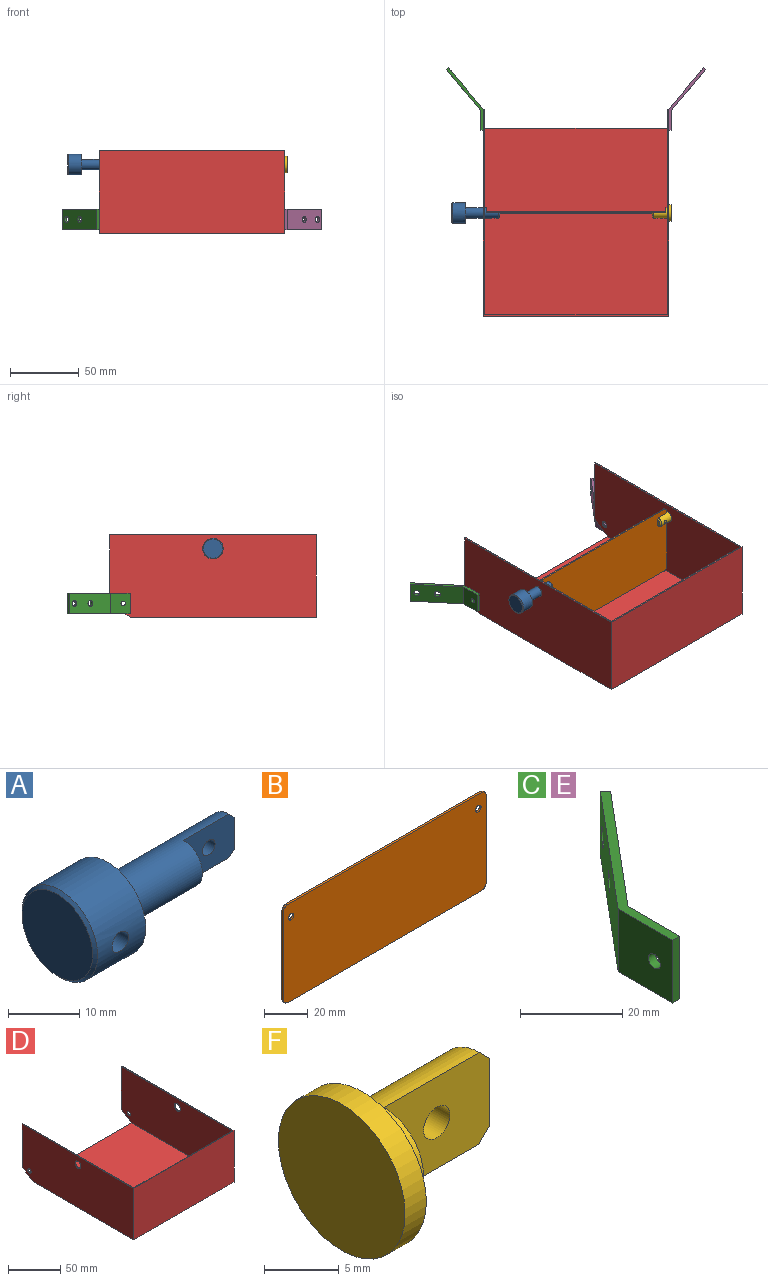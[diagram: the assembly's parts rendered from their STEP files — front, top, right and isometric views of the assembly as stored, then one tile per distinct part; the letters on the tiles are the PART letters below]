
ASSEMBLY  parts=6 mates=5
PART A: 12 faces, bbox 35x15x15 mm
  f0: cylinder r=7.5mm len=15mm, axis (-1,0,0), area 439.1mm2, adj f2,f9,f11
  f1: cylinder r=3.75mm len=24mm, axis (-1,0,0), area 454.5mm2, adj f2,f5,f6,f7,f8
  f2: plane 15x15mm, normal (1,0,0), area 132.5mm2, adj f0,f1
  f3: plane 14x14mm, normal (-1,0,0), area 153.9mm2, adj f11
  f4: plane 5.5x2.75mm, normal (1,0,0), area 11.9mm2, adj f5,f7
  f5: cone r=2.75mm half-angle=45deg, axis (-1,0,0), area 14.4mm2, adj f1,f4,f7
  f6: plane 7.5x3.75mm, normal (1,0,0), area 22.1mm2, adj f1,f7
  f7: plane 10x7.5mm, normal (0,-1,0), area 69.1mm2, adj f1,f4,f5,f6,f8
  f8: cylinder r=1.25mm len=3.75mm, axis (0,-1,0), area 28.6mm2, adj f1,f7
  f9: cylinder r=1.65mm len=7.5mm, axis (0,1,0), area 76.8mm2, adj f0,f10
  f10: plane 3.3x3.3mm, normal (0,-1,0), area 8.6mm2, adj f9
  f11: cone r=7.5mm half-angle=45deg, axis (1,0,0), area 32.2mm2, adj f0,f3
PART B: 12 faces, bbox 131x1x55 mm
  f0: plane 49x1mm, normal (-1,0,0), area 49mm2, adj f4,f5,f6,f9
  f1: plane 125x1mm, normal (0,0,-1), area 125mm2, adj f4,f5,f6,f7
  f2: plane 49x1mm, normal (1,0,0), area 49mm2, adj f4,f5,f7,f8
  f3: plane 125x1mm, normal (0,0,1), area 125mm2, adj f4,f5,f8,f9
  f4: plane 131x55mm, normal (0,-1,0), area 7178mm2, adj f0,f1,f2,f3,f6,f7,f8,f9
  f5: plane 131x55mm, normal (0,1,0), area 7178mm2, adj f0,f1,f2,f3,f6,f7,f8,f9
  f6: cylinder r=3mm len=3mm, axis (0,-1,0), area 4.7mm2, adj f0,f1,f4,f5
  f7: cylinder r=3mm len=3mm, axis (0,-1,0), area 4.7mm2, adj f1,f2,f4,f5
  f8: cylinder r=3mm len=3mm, axis (0,1,0), area 4.7mm2, adj f2,f3,f4,f5
  f9: cylinder r=3mm len=3mm, axis (0,1,0), area 4.7mm2, adj f0,f3,f4,f5
  f10: cylinder r=1.75mm len=3.5mm, axis (0,-1,0), area 11mm2, adj f4,f5
  f11: cylinder r=1.75mm len=3.5mm, axis (0,-1,0), area 11mm2, adj f4,f5
PART C: 11 faces, bbox 27.2x45.6x15 mm
  f0: plane 15x2mm, normal (0,-1,0), area 30mm2, adj f1,f5,f6,f7
  f1: plane 15x14.27mm, normal (1,0,0), area 205.5mm2, adj f0,f2,f6,f7,f8
  f2: plane 30.08x25.24mm, normal (0.77,-0.64,0), area 558.7mm2, adj f1,f3,f6,f7,f9,f10
  f3: plane 15x1.53mm, normal (0.64,0.77,0), area 30mm2, adj f2,f4,f6,f7
  f4: plane 30.64x25.71mm, normal (-0.77,0.64,0), area 569.6mm2, adj f3,f5,f6,f7,f9,f10
  f5: plane 15x15mm, normal (-1,0,0), area 216.4mm2, adj f0,f4,f6,f7,f8
  f6: plane 45.64x27.24mm, normal (0,0,1), area 108.5mm2, adj f0,f1,f2,f3,f4,f5
  f7: plane 45.64x27.24mm, normal (0,0,-1), area 108.5mm2, adj f0,f1,f2,f3,f4,f5
  f8: cylinder r=1.65mm len=3.3mm, axis (1,0,0), area 20.7mm2, adj f1,f5
  f9: cylinder r=2.2mm len=4.66mm, axis (0.77,-0.64,0), area 27.6mm2, adj f2,f4
  f10: cylinder r=2.2mm len=4.66mm, axis (0.77,-0.64,0), area 27.6mm2, adj f2,f4
PART D: 16 faces, bbox 135x151x60 mm
  f0: plane 136x135mm, normal (0,0,-1), area 18360mm2, adj f1,f5,f10,f15
  f1: plane 151x60mm, normal (1,0,0), area 8918.8mm2, adj f0,f7,f8,f10,f11,f13,f15
  f2: plane 150x59mm, normal (-1,0,0), area 8723.1mm2, adj f3,f7,f8,f9,f11,f13,f15
  f3: plane 136.5x133mm, normal (0,0,1), area 18154.5mm2, adj f2,f4,f9,f15
  f4: plane 150x59mm, normal (1,0,0), area 8723.1mm2, adj f3,f6,f8,f9,f12,f14,f15
  f5: plane 151x60mm, normal (-1,0,0), area 8918.8mm2, adj f0,f6,f8,f10,f12,f14,f15
  f6: plane 50x1mm, normal (0,1,0), area 50mm2, adj f4,f5,f8,f15
  f7: plane 50x1mm, normal (0,1,0), area 50mm2, adj f1,f2,f8,f15
  f8: plane 151x135mm, normal (0,0,1), area 435mm2, adj f1,f2,f4,f5,f6,f7,f9,f10
  f9: plane 133x59mm, normal (0,1,0), area 7847mm2, adj f2,f3,f4,f8
  f10: plane 135x60mm, normal (0,-1,0), area 8100mm2, adj f0,f1,f5,f8
  f11: cylinder r=2.25mm len=4.5mm, axis (-1,0,0), area 14.1mm2, adj f1,f2
  f12: cylinder r=2.25mm len=4.5mm, axis (-1,0,0), area 14.1mm2, adj f4,f5
  f13: cylinder r=4mm len=8mm, axis (-1,0,0), area 25.1mm2, adj f1,f2
  f14: cylinder r=4mm len=8mm, axis (-1,0,0), area 25.1mm2, adj f4,f5
  f15: plane 135x15mm, normal (0,0.55,-0.83), area 275.8mm2, adj f0,f1,f2,f3,f4,f5,f6,f7
PART E: same geometry as C
PART F: 9 faces, bbox 14x12x12 mm
  f0: cylinder r=3.75mm len=11mm, axis (-1,0,0), area 148.2mm2, adj f2,f5,f6,f7,f8
  f1: cylinder r=6mm len=12mm, axis (-1,0,0), area 75.4mm2, adj f2,f3
  f2: plane 12x12mm, normal (1,0,0), area 68.9mm2, adj f0,f1
  f3: plane 12x12mm, normal (-1,0,0), area 113.1mm2, adj f1
  f4: plane 5.5x2.75mm, normal (1,0,0), area 11.9mm2, adj f6,f8
  f5: plane 7.5x3.75mm, normal (1,0,0), area 22.1mm2, adj f0,f6
  f6: plane 10x7.5mm, normal (0,-1,0), area 69.1mm2, adj f0,f4,f5,f7,f8
  f7: cylinder r=1.25mm len=3.75mm, axis (0,-1,0), area 28.6mm2, adj f0,f6
  f8: cone r=2.75mm half-angle=45deg, axis (-1,0,0), area 14.4mm2, adj f0,f4,f6
PLACE A rot(axis=(1,0,0),180deg) t=(-90.5,7.5,50)mm
PLACE B t=(0,8.5,30.5)mm
PLACE C rot(axis=(0,1,0),180deg) t=(-69.5,75.65,10)mm
PLACE D t=(0,83,20)mm
PLACE E t=(69.5,75.65,10)mm
PLACE F rot(axis=(0,0,1),180deg) t=(69.5,7.5,50)mm
MATE revolute F.f0 <-> D.f13  axis (-1,0,0) through (67.5,7.5,50)mm
MATE fastened C.f8 <-> D.f11  axis (1,0,0) through (-67.5,73,10)mm
MATE fastened B.f11 <-> F.f7  axis (0,-1,0) through (60.5,7.5,50)mm
MATE fastened A.f8 <-> B.f10  axis (0,1,0) through (-60.5,7.5,50)mm
MATE fastened E.f8 <-> D.f11  axis (-1,0,0) through (67.5,73,10)mm
